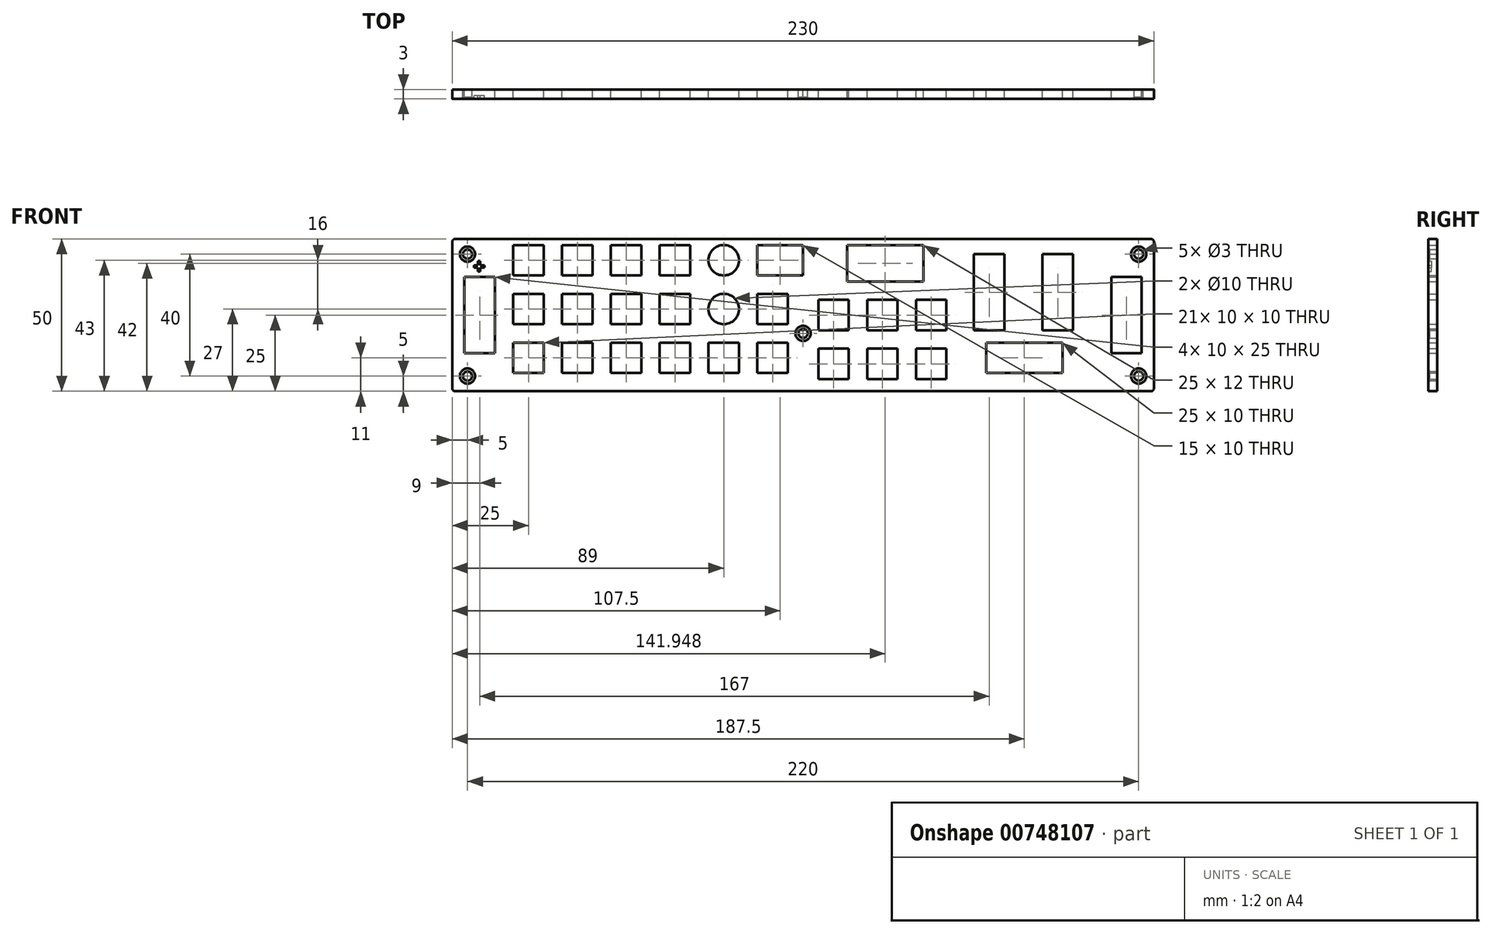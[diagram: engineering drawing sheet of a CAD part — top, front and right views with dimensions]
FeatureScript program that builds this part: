
annotation { "Feature Type Name" : "Feature", "Feature Type Description" : "" }
export const myFeature = defineFeature(function(context is Context, id is Id, definition is map)
    precondition{}
    {
        {
            var Q0;
            Q0=qCreatedBy(makeId("Front.planeOp"),FACE);
            var sketch = newSketch(context, id + "F0", { "sketchPlane" : qUnion([Q0])});
            skLineSegment(sketch, "E0.bottom", {"start": v(115, -16) * mm, "end": v(-115, -16) * mm});
            skLineSegment(sketch, "E0.top", {"start": v(115, 34) * mm, "end": v(-115, 34) * mm});
            skLineSegment(sketch, "E0.left", {"start": v(115, -16) * mm, "end": v(115, 34) * mm});
            skLineSegment(sketch, "E0.right", {"start": v(-115, -16) * mm, "end": v(-115, 34) * mm});
            skLineSegment(sketch, "E1.bottom", {"start": v(-111, 21.5) * mm, "end": v(-101, 21.5) * mm});
            skLineSegment(sketch, "E1.top", {"start": v(-111, -3.5) * mm, "end": v(-101, -3.5) * mm});
            skLineSegment(sketch, "E1.left", {"start": v(-111, 21.5) * mm, "end": v(-111, -3.5) * mm});
            skLineSegment(sketch, "E1.right", {"start": v(-101, 21.5) * mm, "end": v(-101, -3.5) * mm});
            skLineSegment(sketch, "E2.bottom", {"start": v(-95, 32) * mm, "end": v(-85, 32) * mm});
            skLineSegment(sketch, "E2.top", {"start": v(-95, 22) * mm, "end": v(-85, 22) * mm});
            skLineSegment(sketch, "E2.left", {"start": v(-95, 32) * mm, "end": v(-95, 22) * mm});
            skLineSegment(sketch, "E2.right", {"start": v(-85, 32) * mm, "end": v(-85, 22) * mm});
            skLineSegment(sketch, "E3.bottom", {"start": v(-95, 16) * mm, "end": v(-85, 16) * mm});
            skLineSegment(sketch, "E3.top", {"start": v(-95, 6) * mm, "end": v(-85, 6) * mm});
            skLineSegment(sketch, "E3.left", {"start": v(-95, 16) * mm, "end": v(-95, 6) * mm});
            skLineSegment(sketch, "E3.right", {"start": v(-85, 16) * mm, "end": v(-85, 6) * mm});
            skLineSegment(sketch, "E4.bottom", {"start": v(-95, 0) * mm, "end": v(-85, 0) * mm});
            skLineSegment(sketch, "E4.top", {"start": v(-95, -10) * mm, "end": v(-85, -10) * mm});
            skLineSegment(sketch, "E4.left", {"start": v(-95, 0) * mm, "end": v(-95, -10) * mm});
            skLineSegment(sketch, "E4.right", {"start": v(-85, 0) * mm, "end": v(-85, -10) * mm});
            skLineSegment(sketch, "E5", {"start": v(0, 34) * mm, "end": v(0, -16) * mm, "construction": true});
            skPoint(sketch, "E6.endSnap0", {"position": v(-106, -3.5) * mm});
            skLineSegment(sketch, "E7.bottom", {"start": v(-79, 32) * mm, "end": v(-69, 32) * mm});
            skLineSegment(sketch, "E7.top", {"start": v(-79, 22) * mm, "end": v(-69, 22) * mm});
            skLineSegment(sketch, "E7.left", {"start": v(-79, 32) * mm, "end": v(-79, 22) * mm});
            skLineSegment(sketch, "E7.right", {"start": v(-69, 32) * mm, "end": v(-69, 22) * mm});
            skLineSegment(sketch, "E8.bottom", {"start": v(-79, 16) * mm, "end": v(-69, 16) * mm});
            skLineSegment(sketch, "E8.top", {"start": v(-79, 6) * mm, "end": v(-69, 6) * mm});
            skLineSegment(sketch, "E8.left", {"start": v(-79, 16) * mm, "end": v(-79, 6) * mm});
            skLineSegment(sketch, "E8.right", {"start": v(-69, 16) * mm, "end": v(-69, 6) * mm});
            skLineSegment(sketch, "E9.bottom", {"start": v(-79, 0) * mm, "end": v(-69, 0) * mm});
            skLineSegment(sketch, "E9.top", {"start": v(-79, -10) * mm, "end": v(-69, -10) * mm});
            skLineSegment(sketch, "E9.left", {"start": v(-79, 0) * mm, "end": v(-79, -10) * mm});
            skLineSegment(sketch, "E9.right", {"start": v(-69, 0) * mm, "end": v(-69, -10) * mm});
            skLineSegment(sketch, "E10.bottom", {"start": v(-63, 32) * mm, "end": v(-53, 32) * mm});
            skLineSegment(sketch, "E10.top", {"start": v(-63, 22) * mm, "end": v(-53, 22) * mm});
            skLineSegment(sketch, "E10.left", {"start": v(-63, 32) * mm, "end": v(-63, 22) * mm});
            skLineSegment(sketch, "E10.right", {"start": v(-53, 32) * mm, "end": v(-53, 22) * mm});
            skLineSegment(sketch, "E11.bottom", {"start": v(-63, 16) * mm, "end": v(-53, 16) * mm});
            skLineSegment(sketch, "E11.top", {"start": v(-63, 6) * mm, "end": v(-53, 6) * mm});
            skLineSegment(sketch, "E11.left", {"start": v(-63, 16) * mm, "end": v(-63, 6) * mm});
            skLineSegment(sketch, "E11.right", {"start": v(-53, 16) * mm, "end": v(-53, 6) * mm});
            skLineSegment(sketch, "E12.bottom", {"start": v(-63, 0) * mm, "end": v(-53, 0) * mm});
            skLineSegment(sketch, "E12.top", {"start": v(-63, -10) * mm, "end": v(-53, -10) * mm});
            skLineSegment(sketch, "E12.left", {"start": v(-63, 0) * mm, "end": v(-63, -10) * mm});
            skLineSegment(sketch, "E12.right", {"start": v(-53, 0) * mm, "end": v(-53, -10) * mm});
            skLineSegment(sketch, "E13.bottom", {"start": v(-47, 32) * mm, "end": v(-37, 32) * mm});
            skLineSegment(sketch, "E13.top", {"start": v(-47, 22) * mm, "end": v(-37, 22) * mm});
            skLineSegment(sketch, "E13.left", {"start": v(-47, 32) * mm, "end": v(-47, 22) * mm});
            skLineSegment(sketch, "E13.right", {"start": v(-37, 32) * mm, "end": v(-37, 22) * mm});
            skLineSegment(sketch, "E14.bottom", {"start": v(-47, 16) * mm, "end": v(-37, 16) * mm});
            skLineSegment(sketch, "E14.top", {"start": v(-47, 6) * mm, "end": v(-37, 6) * mm});
            skLineSegment(sketch, "E14.left", {"start": v(-47, 16) * mm, "end": v(-47, 6) * mm});
            skLineSegment(sketch, "E14.right", {"start": v(-37, 16) * mm, "end": v(-37, 6) * mm});
            skLineSegment(sketch, "E15.bottom", {"start": v(-47, 0) * mm, "end": v(-37, 0) * mm});
            skLineSegment(sketch, "E15.top", {"start": v(-47, -10) * mm, "end": v(-37, -10) * mm});
            skLineSegment(sketch, "E15.left", {"start": v(-47, 0) * mm, "end": v(-47, -10) * mm});
            skLineSegment(sketch, "E15.right", {"start": v(-37, 0) * mm, "end": v(-37, -10) * mm});
            skCircle(sketch, "E16", {"center": v(-26, 27) * mm, "radius": 5 * mm});
            skCircle(sketch, "E17", {"center": v(-26, 11) * mm, "radius": 5 * mm});
            skLineSegment(sketch, "E18.bottom", {"start": v(-31, 0) * mm, "end": v(-21, 0) * mm});
            skLineSegment(sketch, "E18.top", {"start": v(-31, -10) * mm, "end": v(-21, -10) * mm});
            skLineSegment(sketch, "E18.left", {"start": v(-31, 0) * mm, "end": v(-31, -10) * mm});
            skLineSegment(sketch, "E18.right", {"start": v(-21, 0) * mm, "end": v(-21, -10) * mm});
            skLineSegment(sketch, "E19.bottom", {"start": v(-15, 0) * mm, "end": v(-5, 0) * mm});
            skLineSegment(sketch, "E19.top", {"start": v(-15, -10) * mm, "end": v(-5, -10) * mm});
            skLineSegment(sketch, "E19.left", {"start": v(-15, 0) * mm, "end": v(-15, -10) * mm});
            skLineSegment(sketch, "E19.right", {"start": v(-5, 0) * mm, "end": v(-5, -10) * mm});
            skLineSegment(sketch, "E20.bottom", {"start": v(-15, 16) * mm, "end": v(-5, 16) * mm});
            skLineSegment(sketch, "E20.top", {"start": v(-15, 6) * mm, "end": v(-5, 6) * mm});
            skLineSegment(sketch, "E20.left", {"start": v(-15, 16) * mm, "end": v(-15, 6) * mm});
            skLineSegment(sketch, "E20.right", {"start": v(-5, 16) * mm, "end": v(-5, 6) * mm});
            skLineSegment(sketch, "E21.bottom", {"start": v(-15, 32) * mm, "end": v(0, 32) * mm});
            skLineSegment(sketch, "E21.top", {"start": v(-15, 22) * mm, "end": v(0, 22) * mm});
            skLineSegment(sketch, "E21.left", {"start": v(-15, 32) * mm, "end": v(-15, 22) * mm});
            skLineSegment(sketch, "E21.right", {"start": v(0, 32) * mm, "end": v(0, 22) * mm});
            skLineSegment(sketch, "E22.bottom", {"start": v(101, 21.5) * mm, "end": v(111, 21.5) * mm});
            skLineSegment(sketch, "E22.top", {"start": v(101, -3.5) * mm, "end": v(111, -3.5) * mm});
            skLineSegment(sketch, "E22.left", {"start": v(101, 21.5) * mm, "end": v(101, -3.5) * mm});
            skLineSegment(sketch, "E22.right", {"start": v(111, 21.5) * mm, "end": v(111, -3.5) * mm});
            skLineSegment(sketch, "E23.bottom", {"start": v(60, 0) * mm, "end": v(85, 0) * mm});
            skLineSegment(sketch, "E23.top", {"start": v(60, -10) * mm, "end": v(85, -10) * mm});
            skLineSegment(sketch, "E23.left", {"start": v(60, 0) * mm, "end": v(60, -10) * mm});
            skLineSegment(sketch, "E23.right", {"start": v(85, 0) * mm, "end": v(85, -10) * mm});
            skLineSegment(sketch, "E24.bottom", {"start": v(78.5, 29) * mm, "end": v(88.5, 29) * mm});
            skLineSegment(sketch, "E24.top", {"start": v(78.5, 4) * mm, "end": v(88.5, 4) * mm});
            skLineSegment(sketch, "E24.left", {"start": v(78.5, 29) * mm, "end": v(78.5, 4) * mm});
            skLineSegment(sketch, "E24.right", {"start": v(88.5, 29) * mm, "end": v(88.5, 4) * mm});
            skLineSegment(sketch, "E25.bottom", {"start": v(56, 29) * mm, "end": v(66, 29) * mm});
            skLineSegment(sketch, "E25.top", {"start": v(56, 4) * mm, "end": v(66, 4) * mm});
            skLineSegment(sketch, "E25.left", {"start": v(56, 29) * mm, "end": v(56, 4) * mm});
            skLineSegment(sketch, "E25.right", {"start": v(66, 29) * mm, "end": v(66, 4) * mm});
            skLineSegment(sketch, "E26.bottom", {"start": v(5, -2) * mm, "end": v(15, -2) * mm});
            skLineSegment(sketch, "E26.top", {"start": v(5, -12) * mm, "end": v(15, -12) * mm});
            skLineSegment(sketch, "E26.left", {"start": v(5, -2) * mm, "end": v(5, -12) * mm});
            skLineSegment(sketch, "E26.right", {"start": v(15, -2) * mm, "end": v(15, -12) * mm});
            skLineSegment(sketch, "E27.bottom", {"start": v(21, -2) * mm, "end": v(31, -2) * mm});
            skLineSegment(sketch, "E27.top", {"start": v(21, -12) * mm, "end": v(31, -12) * mm});
            skLineSegment(sketch, "E27.left", {"start": v(21, -2) * mm, "end": v(21, -12) * mm});
            skLineSegment(sketch, "E27.right", {"start": v(31, -2) * mm, "end": v(31, -12) * mm});
            skLineSegment(sketch, "E28.bottom", {"start": v(37, -2) * mm, "end": v(47, -2) * mm});
            skLineSegment(sketch, "E28.top", {"start": v(37, -12) * mm, "end": v(47, -12) * mm});
            skLineSegment(sketch, "E28.left", {"start": v(37, -2) * mm, "end": v(37, -12) * mm});
            skLineSegment(sketch, "E28.right", {"start": v(47, -2) * mm, "end": v(47, -12) * mm});
            skLineSegment(sketch, "E29.bottom", {"start": v(5, 14) * mm, "end": v(15, 14) * mm});
            skLineSegment(sketch, "E29.top", {"start": v(5, 4) * mm, "end": v(15, 4) * mm});
            skLineSegment(sketch, "E29.left", {"start": v(5, 14) * mm, "end": v(5, 4) * mm});
            skLineSegment(sketch, "E29.right", {"start": v(15, 14) * mm, "end": v(15, 4) * mm});
            skLineSegment(sketch, "E30.bottom", {"start": v(21, 14) * mm, "end": v(31, 14) * mm});
            skLineSegment(sketch, "E30.top", {"start": v(21, 4) * mm, "end": v(31, 4) * mm});
            skLineSegment(sketch, "E30.left", {"start": v(21, 14) * mm, "end": v(21, 4) * mm});
            skLineSegment(sketch, "E30.right", {"start": v(31, 14) * mm, "end": v(31, 4) * mm});
            skLineSegment(sketch, "E31.bottom", {"start": v(37, 14) * mm, "end": v(47, 14) * mm});
            skLineSegment(sketch, "E31.top", {"start": v(37, 4) * mm, "end": v(47, 4) * mm});
            skLineSegment(sketch, "E31.left", {"start": v(37, 14) * mm, "end": v(37, 4) * mm});
            skLineSegment(sketch, "E31.right", {"start": v(47, 14) * mm, "end": v(47, 4) * mm});
            skLineSegment(sketch, "E32.bottom", {"start": v(14.45, 32) * mm, "end": v(39.45, 32) * mm});
            skLineSegment(sketch, "E32.top", {"start": v(14.45, 20) * mm, "end": v(39.45, 20) * mm});
            skLineSegment(sketch, "E32.left", {"start": v(14.45, 32) * mm, "end": v(14.45, 20) * mm});
            skLineSegment(sketch, "E32.right", {"start": v(39.45, 32) * mm, "end": v(39.45, 20) * mm});
            skCircle(sketch, "E33", {"center": v(-110, 29) * mm, "radius": 1.5 * mm});
            skCircle(sketch, "E34", {"center": v(-110, -11) * mm, "radius": 1.5 * mm});
            skCircle(sketch, "E35", {"center": v(0, 3) * mm, "radius": 1.5 * mm});
            skCircle(sketch, "E36", {"center": v(110, -11) * mm, "radius": 1.5 * mm});
            skCircle(sketch, "E37", {"center": v(110, 29) * mm, "radius": 1.5 * mm});
            skSolve(sketch);
        }
        {
            var Q0;
            Q0=makeQuery(id+"F0.imprint","IMPRINT",FACE,{"disambiguationData":[TD([[makeQuery(id+"F0.imprint","IMPRINT",EDGE,{"derivedFrom":sQuery(id+"F0.wireOp",EDGE,"E0.bottom")}),-1.0]])]});
            extrude(context, id + "F1", {"entities" : qUnion([Q0]), "depth" : 3 * mm, "offsetDistance" : 25 * mm});
        }
        {
            var Q0;
            Q0=makeQuery(id+"F1.opExtrude","CAP_EDGE",EDGE,{"disambiguationData":[OSD([sQuery(id+"F0.wireOp",EDGE,"E33")])],"isStart":false});
            var Q1;
            Q1=makeQuery(id+"F1.opExtrude","CAP_EDGE",EDGE,{"disambiguationData":[OSD([sQuery(id+"F0.wireOp",EDGE,"E34")])],"isStart":false});
            var Q2;
            Q2=makeQuery(id+"F1.opExtrude","CAP_EDGE",EDGE,{"disambiguationData":[OSD([sQuery(id+"F0.wireOp",EDGE,"E35")])],"isStart":false});
            var Q3;
            Q3=makeQuery(id+"F1.opExtrude","CAP_EDGE",EDGE,{"disambiguationData":[OSD([sQuery(id+"F0.wireOp",EDGE,"E36")])],"isStart":false});
            var Q4;
            Q4=makeQuery(id+"F1.opExtrude","CAP_EDGE",EDGE,{"disambiguationData":[OSD([sQuery(id+"F0.wireOp",EDGE,"E37")])],"isStart":false});
            chamfer(context, id + "F2", {"entities" : qUnion([Q0, Q1, Q2, Q3, Q4]), "chamferType" : ChamferType.TWO_OFFSETS, "width1" : 0.5 * mm, "oppositeDirection" : false, "width2" : 1 * mm, "tangentPropagation" : true});
        }
        {
            var Q0;
            Q0=makeQuery(id+"F1.opExtrude","SWEPT_EDGE",EDGE,{"disambiguationData":[OSD([sQuery(id+"F0.wireOp",EDGE,"E0.top"),sQuery(id+"F0.wireOp",EDGE,"E0.right")])]});
            var Q1;
            Q1=makeQuery(id+"F1.opExtrude","SWEPT_EDGE",EDGE,{"disambiguationData":[OSD([sQuery(id+"F0.wireOp",EDGE,"E0.bottom"),sQuery(id+"F0.wireOp",EDGE,"E0.right")])]});
            var Q2;
            Q2=makeQuery(id+"F1.opExtrude","SWEPT_EDGE",EDGE,{"disambiguationData":[OSD([sQuery(id+"F0.wireOp",EDGE,"E0.bottom"),sQuery(id+"F0.wireOp",EDGE,"E0.left")])]});
            var Q3;
            Q3=makeQuery(id+"F1.opExtrude","SWEPT_EDGE",EDGE,{"disambiguationData":[OSD([sQuery(id+"F0.wireOp",EDGE,"E0.top"),sQuery(id+"F0.wireOp",EDGE,"E0.left")])]});
            fillet(context, id + "F3", {"entities" : qUnion([Q0, Q1, Q2, Q3]), "radius" : 1 * mm, "tangentPropagation" : true, "allowEdgeOverflow" : false});
        }
        {
            var Q0;
            Q0=makeQuery(id+"F1.opExtrude","CAP_FACE",FACE,{"disambiguationData":[OSD([sQuery(id+"F0.wireOp",EDGE,"E0.bottom"),sQuery(id+"F0.wireOp",EDGE,"E0.top"),sQuery(id+"F0.wireOp",EDGE,"E0.left"),sQuery(id+"F0.wireOp",EDGE,"E0.right"),sQuery(id+"F0.wireOp",EDGE,"E1.bottom"),sQuery(id+"F0.wireOp",EDGE,"E1.top"),sQuery(id+"F0.wireOp",EDGE,"E1.left"),sQuery(id+"F0.wireOp",EDGE,"E1.right"),sQuery(id+"F0.wireOp",EDGE,"E2.bottom"),sQuery(id+"F0.wireOp",EDGE,"E2.top"),sQuery(id+"F0.wireOp",EDGE,"E2.left"),sQuery(id+"F0.wireOp",EDGE,"E2.right"),sQuery(id+"F0.wireOp",EDGE,"E3.bottom"),sQuery(id+"F0.wireOp",EDGE,"E3.top"),sQuery(id+"F0.wireOp",EDGE,"E3.left"),sQuery(id+"F0.wireOp",EDGE,"E3.right"),sQuery(id+"F0.wireOp",EDGE,"E4.bottom"),sQuery(id+"F0.wireOp",EDGE,"E4.top"),sQuery(id+"F0.wireOp",EDGE,"E4.left"),sQuery(id+"F0.wireOp",EDGE,"E4.right"),sQuery(id+"F0.wireOp",EDGE,"E7.bottom"),sQuery(id+"F0.wireOp",EDGE,"E7.top"),sQuery(id+"F0.wireOp",EDGE,"E7.left"),sQuery(id+"F0.wireOp",EDGE,"E7.right"),sQuery(id+"F0.wireOp",EDGE,"E8.bottom"),sQuery(id+"F0.wireOp",EDGE,"E8.top"),sQuery(id+"F0.wireOp",EDGE,"E8.left"),sQuery(id+"F0.wireOp",EDGE,"E8.right"),sQuery(id+"F0.wireOp",EDGE,"E9.bottom"),sQuery(id+"F0.wireOp",EDGE,"E9.top"),sQuery(id+"F0.wireOp",EDGE,"E9.left"),sQuery(id+"F0.wireOp",EDGE,"E9.right"),sQuery(id+"F0.wireOp",EDGE,"E10.bottom"),sQuery(id+"F0.wireOp",EDGE,"E10.top"),sQuery(id+"F0.wireOp",EDGE,"E10.left"),sQuery(id+"F0.wireOp",EDGE,"E10.right"),sQuery(id+"F0.wireOp",EDGE,"E11.bottom"),sQuery(id+"F0.wireOp",EDGE,"E11.top"),sQuery(id+"F0.wireOp",EDGE,"E11.left"),sQuery(id+"F0.wireOp",EDGE,"E11.right"),sQuery(id+"F0.wireOp",EDGE,"E12.bottom"),sQuery(id+"F0.wireOp",EDGE,"E12.top"),sQuery(id+"F0.wireOp",EDGE,"E12.left"),sQuery(id+"F0.wireOp",EDGE,"E12.right"),sQuery(id+"F0.wireOp",EDGE,"E13.bottom"),sQuery(id+"F0.wireOp",EDGE,"E13.top"),sQuery(id+"F0.wireOp",EDGE,"E13.left"),sQuery(id+"F0.wireOp",EDGE,"E13.right"),sQuery(id+"F0.wireOp",EDGE,"E14.bottom"),sQuery(id+"F0.wireOp",EDGE,"E14.top"),sQuery(id+"F0.wireOp",EDGE,"E14.left"),sQuery(id+"F0.wireOp",EDGE,"E14.right"),sQuery(id+"F0.wireOp",EDGE,"E15.bottom"),sQuery(id+"F0.wireOp",EDGE,"E15.top"),sQuery(id+"F0.wireOp",EDGE,"E15.left"),sQuery(id+"F0.wireOp",EDGE,"E15.right"),sQuery(id+"F0.wireOp",EDGE,"E16"),sQuery(id+"F0.wireOp",EDGE,"E17"),sQuery(id+"F0.wireOp",EDGE,"E18.bottom"),sQuery(id+"F0.wireOp",EDGE,"E18.top"),sQuery(id+"F0.wireOp",EDGE,"E18.left"),sQuery(id+"F0.wireOp",EDGE,"E18.right"),sQuery(id+"F0.wireOp",EDGE,"E19.bottom"),sQuery(id+"F0.wireOp",EDGE,"E19.top"),sQuery(id+"F0.wireOp",EDGE,"E19.left"),sQuery(id+"F0.wireOp",EDGE,"E19.right"),sQuery(id+"F0.wireOp",EDGE,"E20.bottom"),sQuery(id+"F0.wireOp",EDGE,"E20.top"),sQuery(id+"F0.wireOp",EDGE,"E20.left"),sQuery(id+"F0.wireOp",EDGE,"E20.right"),sQuery(id+"F0.wireOp",EDGE,"E21.bottom"),sQuery(id+"F0.wireOp",EDGE,"E21.top"),sQuery(id+"F0.wireOp",EDGE,"E21.left"),sQuery(id+"F0.wireOp",EDGE,"E21.right"),sQuery(id+"F0.wireOp",EDGE,"E22.bottom"),sQuery(id+"F0.wireOp",EDGE,"E22.top"),sQuery(id+"F0.wireOp",EDGE,"E22.left"),sQuery(id+"F0.wireOp",EDGE,"E22.right"),sQuery(id+"F0.wireOp",EDGE,"E23.bottom"),sQuery(id+"F0.wireOp",EDGE,"E23.top"),sQuery(id+"F0.wireOp",EDGE,"E23.left"),sQuery(id+"F0.wireOp",EDGE,"E23.right"),sQuery(id+"F0.wireOp",EDGE,"E24.bottom"),sQuery(id+"F0.wireOp",EDGE,"E24.top"),sQuery(id+"F0.wireOp",EDGE,"E24.left"),sQuery(id+"F0.wireOp",EDGE,"E24.right"),sQuery(id+"F0.wireOp",EDGE,"E25.bottom"),sQuery(id+"F0.wireOp",EDGE,"E25.top"),sQuery(id+"F0.wireOp",EDGE,"E25.left"),sQuery(id+"F0.wireOp",EDGE,"E25.right"),sQuery(id+"F0.wireOp",EDGE,"E26.bottom"),sQuery(id+"F0.wireOp",EDGE,"E26.top"),sQuery(id+"F0.wireOp",EDGE,"E26.left"),sQuery(id+"F0.wireOp",EDGE,"E26.right"),sQuery(id+"F0.wireOp",EDGE,"E27.bottom"),sQuery(id+"F0.wireOp",EDGE,"E27.top"),sQuery(id+"F0.wireOp",EDGE,"E27.left"),sQuery(id+"F0.wireOp",EDGE,"E27.right"),sQuery(id+"F0.wireOp",EDGE,"E28.bottom"),sQuery(id+"F0.wireOp",EDGE,"E28.top"),sQuery(id+"F0.wireOp",EDGE,"E28.left"),sQuery(id+"F0.wireOp",EDGE,"E28.right"),sQuery(id+"F0.wireOp",EDGE,"E29.bottom"),sQuery(id+"F0.wireOp",EDGE,"E29.top"),sQuery(id+"F0.wireOp",EDGE,"E29.left"),sQuery(id+"F0.wireOp",EDGE,"E29.right"),sQuery(id+"F0.wireOp",EDGE,"E30.bottom"),sQuery(id+"F0.wireOp",EDGE,"E30.top"),sQuery(id+"F0.wireOp",EDGE,"E30.left"),sQuery(id+"F0.wireOp",EDGE,"E30.right"),sQuery(id+"F0.wireOp",EDGE,"E31.bottom"),sQuery(id+"F0.wireOp",EDGE,"E31.top"),sQuery(id+"F0.wireOp",EDGE,"E31.left"),sQuery(id+"F0.wireOp",EDGE,"E31.right"),sQuery(id+"F0.wireOp",EDGE,"E32.bottom"),sQuery(id+"F0.wireOp",EDGE,"E32.top"),sQuery(id+"F0.wireOp",EDGE,"E32.left"),sQuery(id+"F0.wireOp",EDGE,"E32.right"),sQuery(id+"F0.wireOp",EDGE,"E33"),sQuery(id+"F0.wireOp",EDGE,"E34"),sQuery(id+"F0.wireOp",EDGE,"E35"),sQuery(id+"F0.wireOp",EDGE,"E36"),sQuery(id+"F0.wireOp",EDGE,"E37")])],"isStart":false});
            var sketch = newSketch(context, id + "F4", { "sketchPlane" : qUnion([Q0])});
            skText(sketch, "E38", { "text": "+", "fontName": "OpenSans-Bold.ttf"});
            const initialGuessF4  = {"E38": [-0.10816, 0.0225, 1, 0, 0.00505]};
            skSetInitialGuess(sketch, initialGuessF4);
            skSolve(sketch);
        }
        {
            var Q0;
            Q0=makeQuery(id+"F4.imprint","IMPRINT",FACE,{"disambiguationData":[TD([[makeQuery(id+"F4.imprint","IMPRINT",EDGE,{"derivedFrom":sQuery(id+"F4.wireOp",EDGE,"E38.sketch_text.stroke-0")}),-1.0]])]});
            extrude(context, id + "F5", {"entities" : qUnion([Q0]), "operationType" : NewBodyOperationType.REMOVE, "oppositeDirection" : true, "depth" : 1 * mm, "offsetDistance" : 25 * mm});
        }
        {
            var Q0;
            Q0=makeQuery(id+"F5.boolean.opBoolean","COPY",FACE,{"derivedFrom":makeQuery(id+"F5.opExtrude","CAP_FACE",FACE,{"disambiguationData":[OSD([sQuery(id+"F4.wireOp",EDGE,"E38.sketch_text.stroke-0"),sQuery(id+"F4.wireOp",EDGE,"E38.sketch_text.stroke-1"),sQuery(id+"F4.wireOp",EDGE,"E38.sketch_text.stroke-2"),sQuery(id+"F4.wireOp",EDGE,"E38.sketch_text.stroke-3"),sQuery(id+"F4.wireOp",EDGE,"E38.sketch_text.stroke-4"),sQuery(id+"F4.wireOp",EDGE,"E38.sketch_text.stroke-5"),sQuery(id+"F4.wireOp",EDGE,"E38.sketch_text.stroke-6"),sQuery(id+"F4.wireOp",EDGE,"E38.sketch_text.stroke-7"),sQuery(id+"F4.wireOp",EDGE,"E38.sketch_text.stroke-8"),sQuery(id+"F4.wireOp",EDGE,"E38.sketch_text.stroke-9"),sQuery(id+"F4.wireOp",EDGE,"E38.sketch_text.stroke-10"),sQuery(id+"F4.wireOp",EDGE,"E38.sketch_text.stroke-11")])],"isStart":false})});
            extrude(context, id + "F6", {"entities" : qUnion([Q0]), "depth" : 1 * mm, "offsetDistance" : 25 * mm});
        }
    });
